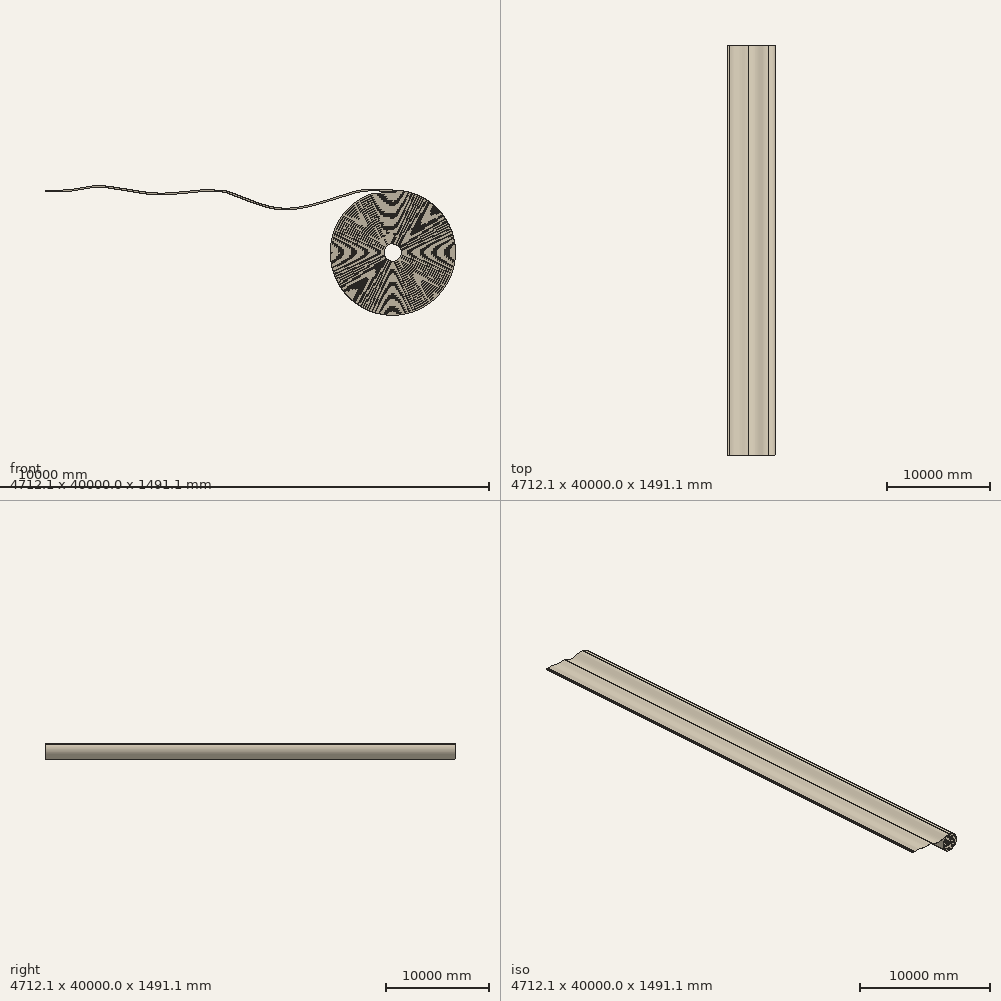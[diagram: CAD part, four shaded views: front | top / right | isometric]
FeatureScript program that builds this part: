
annotation { "Feature Type Name" : "Feature", "Feature Type Description" : "" }
export const myFeature = defineFeature(function(context is Context, id is Id, definition is map)
    precondition{}
    {
        {
            var Q0;
            Q0=qCreatedBy(makeId("Front.planeOp"),FACE);
            var sketch = newSketch(context, id + "F0", { "sketchPlane" : qUnion([Q0])});
            skLineSegment(sketch, "E0", {"start": v(-1454.5, 0) * mm, "end": v(-1268.4, 0) * mm});
            skFitSpline(sketch, "E1", {"points": [v(560.9, 0) * mm, v(1244.24, -205.21) * mm, v(2170.95, 0) * mm, v(2560.9, 0) * mm], "startDerivative": vector(1068.45, 0) * mm, "endDerivative": vector(1156.29, 20.17) * mm});
            skArc(sketch, "E2", {"start": v(2275.52, -50.55) * mm, "mid": v(2659.74, -1388.88) * mm, "end": v(2560.9, 0) * mm});
            skArc(sketch, "E3", {"start": v(2507.44, -604.29) * mm, "mid": v(2538.06, -799.61) * mm, "end": v(2567.1, -604.05) * mm});
            skArc(sketch, "E4", {"start": v(2285.34, -73.55) * mm, "mid": v(2706.31, -1353.2) * mm, "end": v(2455.52, -29.63) * mm});
            skArc(sketch, "E5", {"start": v(2300.24, -94.52) * mm, "mid": v(2693.86, -1330.56) * mm, "end": v(2465.34, -53.65) * mm});
            skArc(sketch, "E6", {"start": v(2327.42, -191.38) * mm, "mid": v(2663.4, -1235.05) * mm, "end": v(2499.68, -150.93) * mm});
            skArc(sketch, "E7", {"start": v(2342.56, -239.25) * mm, "mid": v(2648.33, -1187.21) * mm, "end": v(2514.89, -200.13) * mm});
            skArc(sketch, "E8", {"start": v(2360.2, -286.08) * mm, "mid": v(2631.25, -1139.77) * mm, "end": v(2531.5, -249.66) * mm});
            skArc(sketch, "E9", {"start": v(2302.43, -120.57) * mm, "mid": v(2685.57, -1306.86) * mm, "end": v(2480.24, -77.26) * mm});
            skArc(sketch, "E10", {"start": v(2310.47, -144.29) * mm, "mid": v(2680.42, -1282.38) * mm, "end": v(2482.43, -102.16) * mm});
            skArc(sketch, "E11", {"start": v(2319.68, -167.53) * mm, "mid": v(2671.8, -1258.75) * mm, "end": v(2490.47, -126.55) * mm});
            skArc(sketch, "E12", {"start": v(2334.89, -215.35) * mm, "mid": v(2655.85, -1211.14) * mm, "end": v(2507.42, -175.49) * mm});
            skArc(sketch, "E13", {"start": v(2351.5, -262.61) * mm, "mid": v(2640.04, -1163.45) * mm, "end": v(2522.56, -224.85) * mm});
            skArc(sketch, "E14", {"start": v(2351.51, -317.55) * mm, "mid": v(2631.93, -1114.03) * mm, "end": v(2540.2, -274.62) * mm});
            skArc(sketch, "E15", {"start": v(2377.93, -332.89) * mm, "mid": v(2622.24, -1090.57) * mm, "end": v(2531.51, -299.66) * mm});
            skArc(sketch, "E16", {"start": v(2387.38, -356.04) * mm, "mid": v(2604.46, -1068.61) * mm, "end": v(2557.93, -325.16) * mm});
            skArc(sketch, "E17", {"start": v(2383.28, -385.5) * mm, "mid": v(2602.34, -1043.58) * mm, "end": v(2567.38, -350.88) * mm});
            skArc(sketch, "E18", {"start": v(2396.46, -406.89) * mm, "mid": v(2597.52, -1019.05) * mm, "end": v(2563.28, -375.63) * mm});
            skArc(sketch, "E19", {"start": v(2402.9, -431.58) * mm, "mid": v(2587.83, -995.39) * mm, "end": v(2576.46, -402.13) * mm});
            skArc(sketch, "E20", {"start": v(2407.91, -457.14) * mm, "mid": v(2582.28, -970.97) * mm, "end": v(2582.9, -428.36) * mm});
            skArc(sketch, "E21", {"start": v(2421.19, -478.4) * mm, "mid": v(2572.81, -947.13) * mm, "end": v(2587.91, -454.72) * mm});
            skArc(sketch, "E22", {"start": v(2429.04, -502.57) * mm, "mid": v(2572.28, -921.93) * mm, "end": v(2581.19, -478.87) * mm});
            skArc(sketch, "E23", {"start": v(2425, -534.36) * mm, "mid": v(2555.55, -898.81) * mm, "end": v(2619.04, -516.92) * mm});
            skArc(sketch, "E24", {"start": v(2443.05, -552.39) * mm, "mid": v(2563.56, -872.69) * mm, "end": v(2585, -531.14) * mm});
            skArc(sketch, "E25", {"start": v(2455.27, -574.27) * mm, "mid": v(2558.14, -848.2) * mm, "end": v(2583.05, -556.65) * mm});
            skArc(sketch, "E26", {"start": v(2467.1, -596.43) * mm, "mid": v(2555.97, -823.26) * mm, "end": v(2575.27, -580.4) * mm});
            skFitSpline(sketch, "E27", {"points": [v(2275.52, -50.55) * mm, v(2455.52, -29.63) * mm], "startDerivative": vector(184.04, 64.56) * mm, "endDerivative": vector(153.52, 24.83) * mm});
            skFitSpline(sketch, "E28", {"points": [v(2285.34, -73.55) * mm, v(2465.34, -53.65) * mm], "startDerivative": vector(180.43, 63) * mm, "endDerivative": vector(157.04, 24.1) * mm});
            skFitSpline(sketch, "E29", {"points": [v(2300.24, -94.52) * mm, v(2480.24, -77.26) * mm], "startDerivative": vector(158, 54.3) * mm, "endDerivative": vector(138.8, 26.35) * mm});
            skFitSpline(sketch, "E30", {"points": [v(2302.43, -120.57) * mm, v(2482.43, -102.16) * mm], "startDerivative": vector(147.88, 52.97) * mm, "endDerivative": vector(150.42, 20.33) * mm});
            skFitSpline(sketch, "E31", {"points": [v(2310.47, -144.29) * mm, v(2490.47, -126.55) * mm], "startDerivative": vector(145.62, 52.38) * mm, "endDerivative": vector(143.46, 17.9) * mm});
            skFitSpline(sketch, "E32", {"points": [v(2319.68, -167.53) * mm, v(2499.68, -150.93) * mm], "startDerivative": vector(136.82, 49.42) * mm, "endDerivative": vector(135.7, 15.05) * mm});
            skFitSpline(sketch, "E33", {"points": [v(2327.42, -191.38) * mm, v(2507.42, -175.49) * mm], "startDerivative": vector(141.63, 51.15) * mm, "endDerivative": vector(141.99, 14.67) * mm});
            skFitSpline(sketch, "E34", {"points": [v(2334.89, -215.35) * mm, v(2514.89, -200.13) * mm], "startDerivative": vector(129.33, 47.62) * mm, "endDerivative": vector(125.38, 11) * mm});
            skFitSpline(sketch, "E35", {"points": [v(2342.56, -239.25) * mm, v(2522.56, -224.85) * mm], "startDerivative": vector(119.54, 44.76) * mm, "endDerivative": vector(115.68, 8.4) * mm});
            skFitSpline(sketch, "E36", {"points": [v(2351.5, -262.61) * mm, v(2531.5, -249.66) * mm], "startDerivative": vector(113.4, 42.7) * mm, "endDerivative": vector(114.2, 6.4) * mm});
            skFitSpline(sketch, "E37", {"points": [v(2360.2, -286.08) * mm, v(2540.2, -274.62) * mm], "startDerivative": vector(98.33, 37.73) * mm, "endDerivative": vector(116.37, 4.62) * mm});
            skFitSpline(sketch, "E38", {"points": [v(2351.51, -317.55) * mm, v(2531.51, -299.66) * mm], "startDerivative": vector(95.3, 41.7) * mm, "endDerivative": vector(105.39, 6.26) * mm});
            skFitSpline(sketch, "E39", {"points": [v(2377.93, -332.89) * mm, v(2557.93, -325.16) * mm], "startDerivative": vector(104.74, 39.9) * mm, "endDerivative": vector(99.87, -0.97) * mm});
            skFitSpline(sketch, "E40", {"points": [v(2387.38, -356.04) * mm, v(2567.38, -350.88) * mm], "startDerivative": vector(81.89, 32.07) * mm, "endDerivative": vector(91.09, -3.8) * mm});
            skFitSpline(sketch, "E41", {"points": [v(2383.28, -385.5) * mm, v(2563.28, -375.63) * mm], "startDerivative": vector(84.57, 37.04) * mm, "endDerivative": vector(95.01, -2.87) * mm});
            skFitSpline(sketch, "E42", {"points": [v(2396.46, -406.89) * mm, v(2576.46, -402.13) * mm], "startDerivative": vector(86.06, 36.53) * mm, "endDerivative": vector(82.2, -6.91) * mm});
            skFitSpline(sketch, "E43", {"points": [v(2402.9, -431.58) * mm, v(2582.9, -428.36) * mm], "startDerivative": vector(82.24, 36.32) * mm, "endDerivative": vector(86.15, -9.75) * mm});
            skFitSpline(sketch, "E44", {"points": [v(2407.91, -457.14) * mm, v(2587.91, -454.72) * mm], "startDerivative": vector(80.69, 37.72) * mm, "endDerivative": vector(79.35, -11.9) * mm});
            skFitSpline(sketch, "E45", {"points": [v(2421.19, -478.4) * mm, v(2581.19, -478.87) * mm], "startDerivative": vector(76.5, 34.95) * mm, "endDerivative": vector(71.52, -10.16) * mm});
            skFitSpline(sketch, "E46", {"points": [v(2429.04, -502.57) * mm, v(2619.04, -516.92) * mm], "startDerivative": vector(87.34, 40.31) * mm, "endDerivative": vector(69.76, -26.02) * mm});
            skFitSpline(sketch, "E47", {"points": [v(2425, -534.36) * mm, v(2585, -531.14) * mm], "startDerivative": vector(69.49, 40.82) * mm, "endDerivative": vector(71.47, -14.82) * mm});
            skFitSpline(sketch, "E48", {"points": [v(2443.05, -552.39) * mm, v(2583.05, -556.65) * mm], "startDerivative": vector(68, 36.92) * mm, "endDerivative": vector(71.52, -16.43) * mm});
            skFitSpline(sketch, "E49", {"points": [v(2455.27, -574.27) * mm, v(2575.27, -580.4) * mm], "startDerivative": vector(60.81, 33.56) * mm, "endDerivative": vector(67.74, -14.66) * mm});
            skFitSpline(sketch, "E50", {"points": [v(2467.1, -596.43) * mm, v(2567.1, -604.05) * mm], "startDerivative": vector(53.05, 30.25) * mm, "endDerivative": vector(59.85, -11.94) * mm});
            skFitSpline(sketch, "E51", {"points": [v(560.9, 0) * mm, v(305.76, 0) * mm, v(-208.38, -32.7) * mm, v(-851, 51.44) * mm, v(-1268.4, 0) * mm], "startDerivative": vector(-2021.3, 0) * mm, "endDerivative": vector(-2066.32, 0) * mm});
            skSolve(sketch);
        }
        {
            var Q0;
            Q0=sQuery(id+"F0.wireOp",VERTEX,"E0.start");
            var Q1;
            Q1=qCreatedBy(makeId("Right.planeOp"),FACE);
            cPlane(context, id + "F1", {"entities" : qUnion([Q0, Q1]), "cplaneType" : CPlaneType.PLANE_POINT, "offset" : 25 * mm, "width" : 150 * mm, "height" : 150 * mm});
        }
        {
            var Q0;
            Q0=qCreatedBy(id+"F1.planeOp",FACE);
            var sketch = newSketch(context, id + "F2", { "sketchPlane" : qUnion([Q0])});
            skLineSegment(sketch, "E52.bottom", {"start": v(0, 0) * mm, "end": v(40000, 0) * mm});
            skLineSegment(sketch, "E52.top", {"start": v(0, 20) * mm, "end": v(40000, 20) * mm});
            skLineSegment(sketch, "E52.left", {"start": v(0, 0) * mm, "end": v(0, 20) * mm});
            skLineSegment(sketch, "E52.right", {"start": v(40000, 0) * mm, "end": v(40000, 20) * mm});
            skSolve(sketch);
        }
        {
            var Q0;
            Q0=makeQuery(id+"F2.imprint","IMPRINT",FACE,{"disambiguationData":[TD([[makeQuery(id+"F2.imprint","IMPRINT",EDGE,{"derivedFrom":sQuery(id+"F2.wireOp",EDGE,"E52.bottom")}),1.0]])]});
            var Q1;
            Q1=sQuery(id+"F0.wireOp",EDGE,"E0");
            var Q2;
            Q2=sQuery(id+"F0.wireOp",EDGE,"E1");
            var Q3;
            Q3=sQuery(id+"F0.wireOp",EDGE,"E2");
            var Q4;
            Q4=sQuery(id+"F0.wireOp",EDGE,"E27");
            var Q5;
            Q5=sQuery(id+"F0.wireOp",EDGE,"E4");
            var Q6;
            Q6=sQuery(id+"F0.wireOp",EDGE,"E28");
            var Q7;
            Q7=sQuery(id+"F0.wireOp",EDGE,"E5");
            var Q8;
            Q8=sQuery(id+"F0.wireOp",EDGE,"E29");
            var Q9;
            Q9=sQuery(id+"F0.wireOp",EDGE,"E9");
            var Q10;
            Q10=sQuery(id+"F0.wireOp",EDGE,"E30");
            var Q11;
            Q11=sQuery(id+"F0.wireOp",EDGE,"E10");
            var Q12;
            Q12=sQuery(id+"F0.wireOp",EDGE,"E31");
            var Q13;
            Q13=sQuery(id+"F0.wireOp",EDGE,"E11");
            var Q14;
            Q14=sQuery(id+"F0.wireOp",EDGE,"E32");
            var Q15;
            Q15=sQuery(id+"F0.wireOp",EDGE,"E6");
            var Q16;
            Q16=sQuery(id+"F0.wireOp",EDGE,"E33");
            var Q17;
            Q17=sQuery(id+"F0.wireOp",EDGE,"E12");
            var Q18;
            Q18=sQuery(id+"F0.wireOp",EDGE,"E34");
            var Q19;
            Q19=sQuery(id+"F0.wireOp",EDGE,"E7");
            var Q20;
            Q20=sQuery(id+"F0.wireOp",EDGE,"E35");
            var Q21;
            Q21=sQuery(id+"F0.wireOp",EDGE,"E13");
            var Q22;
            Q22=sQuery(id+"F0.wireOp",EDGE,"E36");
            var Q23;
            Q23=sQuery(id+"F0.wireOp",EDGE,"E8");
            var Q24;
            Q24=sQuery(id+"F0.wireOp",EDGE,"E37");
            var Q25;
            Q25=sQuery(id+"F0.wireOp",EDGE,"E14");
            var Q26;
            Q26=sQuery(id+"F0.wireOp",EDGE,"E38");
            var Q27;
            Q27=sQuery(id+"F0.wireOp",EDGE,"E36");
            var Q28;
            Q28=sQuery(id+"F0.wireOp",EDGE,"E15");
            var Q29;
            Q29=sQuery(id+"F0.wireOp",EDGE,"E39");
            var Q30;
            Q30=sQuery(id+"F0.wireOp",EDGE,"E16");
            var Q31;
            Q31=sQuery(id+"F0.wireOp",EDGE,"E40");
            var Q32;
            Q32=sQuery(id+"F0.wireOp",EDGE,"E17");
            var Q33;
            Q33=sQuery(id+"F0.wireOp",EDGE,"E41");
            var Q34;
            Q34=sQuery(id+"F0.wireOp",EDGE,"E18");
            var Q35;
            Q35=sQuery(id+"F0.wireOp",EDGE,"E42");
            var Q36;
            Q36=sQuery(id+"F0.wireOp",EDGE,"E19");
            var Q37;
            Q37=sQuery(id+"F0.wireOp",EDGE,"E43");
            var Q38;
            Q38=sQuery(id+"F0.wireOp",EDGE,"E20");
            var Q39;
            Q39=sQuery(id+"F0.wireOp",EDGE,"E44");
            var Q40;
            Q40=sQuery(id+"F0.wireOp",EDGE,"E21");
            var Q41;
            Q41=sQuery(id+"F0.wireOp",EDGE,"E45");
            var Q42;
            Q42=sQuery(id+"F0.wireOp",EDGE,"E22");
            var Q43;
            Q43=sQuery(id+"F0.wireOp",EDGE,"E46");
            var Q44;
            Q44=sQuery(id+"F0.wireOp",EDGE,"E23");
            var Q45;
            Q45=sQuery(id+"F0.wireOp",EDGE,"E47");
            var Q46;
            Q46=sQuery(id+"F0.wireOp",EDGE,"E24");
            var Q47;
            Q47=sQuery(id+"F0.wireOp",EDGE,"E48");
            var Q48;
            Q48=sQuery(id+"F0.wireOp",EDGE,"E25");
            var Q49;
            Q49=sQuery(id+"F0.wireOp",EDGE,"E49");
            var Q50;
            Q50=sQuery(id+"F0.wireOp",EDGE,"E26");
            var Q51;
            Q51=sQuery(id+"F0.wireOp",EDGE,"E50");
            var Q52;
            Q52=sQuery(id+"F0.wireOp",EDGE,"E3");
            var Q53;
            Q53=sQuery(id+"F0.wireOp",EDGE,"E51");
            sweep(context, id + "F3", {"profiles" : qUnion([Q0]), "path" : qUnion([Q1, Q2, Q3, Q4, Q5, Q6, Q7, Q8, Q9, Q10, Q11, Q12, Q13, Q14, Q15, Q16, Q17, Q18, Q19, Q20, Q21, Q22, Q23, Q24, Q25, Q26, Q27, Q28, Q29, Q30, Q31, Q32, Q33, Q34, Q35, Q36, Q37, Q38, Q39, Q40, Q41, Q42, Q43, Q44, Q45, Q46, Q47, Q48, Q49, Q50, Q51, Q52, Q53])});
        }
        {
            var Q0;
            Q0=makeQuery(id+"F3.opSweep","SWEPT_FACE",FACE,{"disambiguationData":[OSD([sQuery(id+"F0.wireOp",EDGE,"E0"),sQuery(id+"F2.wireOp",EDGE,"E52.bottom")])]});
            var sketch = newSketch(context, id + "F4", { "sketchPlane" : qUnion([Q0])});
            skCircle(sketch, "E53", {"center": v(-1361.45, -39900) * mm, "radius": 17.5 * mm});
            skPoint(sketch, "E53.centerSnap0", {"position": v(-1361.45, -40000) * mm});
            skCircle(sketch, "E54.0.1.0", {"center": v(-1361.45, -34250) * mm, "radius": 17.5 * mm});
            skCircle(sketch, "E54.0.2.0", {"center": v(-1361.45, -28600) * mm, "radius": 17.5 * mm});
            skCircle(sketch, "E54.0.3.0", {"center": v(-1361.45, -22950) * mm, "radius": 17.5 * mm});
            skCircle(sketch, "E54.0.4.0", {"center": v(-1361.45, -17300) * mm, "radius": 17.5 * mm});
            skCircle(sketch, "E54.0.5.0", {"center": v(-1361.45, -11650) * mm, "radius": 17.5 * mm});
            skCircle(sketch, "E54.0.6.0", {"center": v(-1361.45, -6000) * mm, "radius": 17.5 * mm});
            skCircle(sketch, "E54.0.7.0", {"center": v(-1361.45, -350) * mm, "radius": 17.5 * mm});
            skLineSegment(sketch, "E54.direction1", {"start": v(-1361.45, -39900) * mm, "end": v(-1039.14, -39900) * mm, "construction": true});
            skLineSegment(sketch, "E54.direction2", {"start": v(-1361.45, -39900) * mm, "end": v(-1361.45, -34250) * mm, "construction": true});
            skSolve(sketch);
        }
        {
            var Q0;
            Q0=qSketchRegion(id+"F4",true);
            extrude(context, id + "F5", {"entities" : qUnion([Q0]), "operationType" : NewBodyOperationType.REMOVE, "oppositeDirection" : true, "depth" : 25 * mm, "offsetDistance" : 25 * mm});
        }
    });
